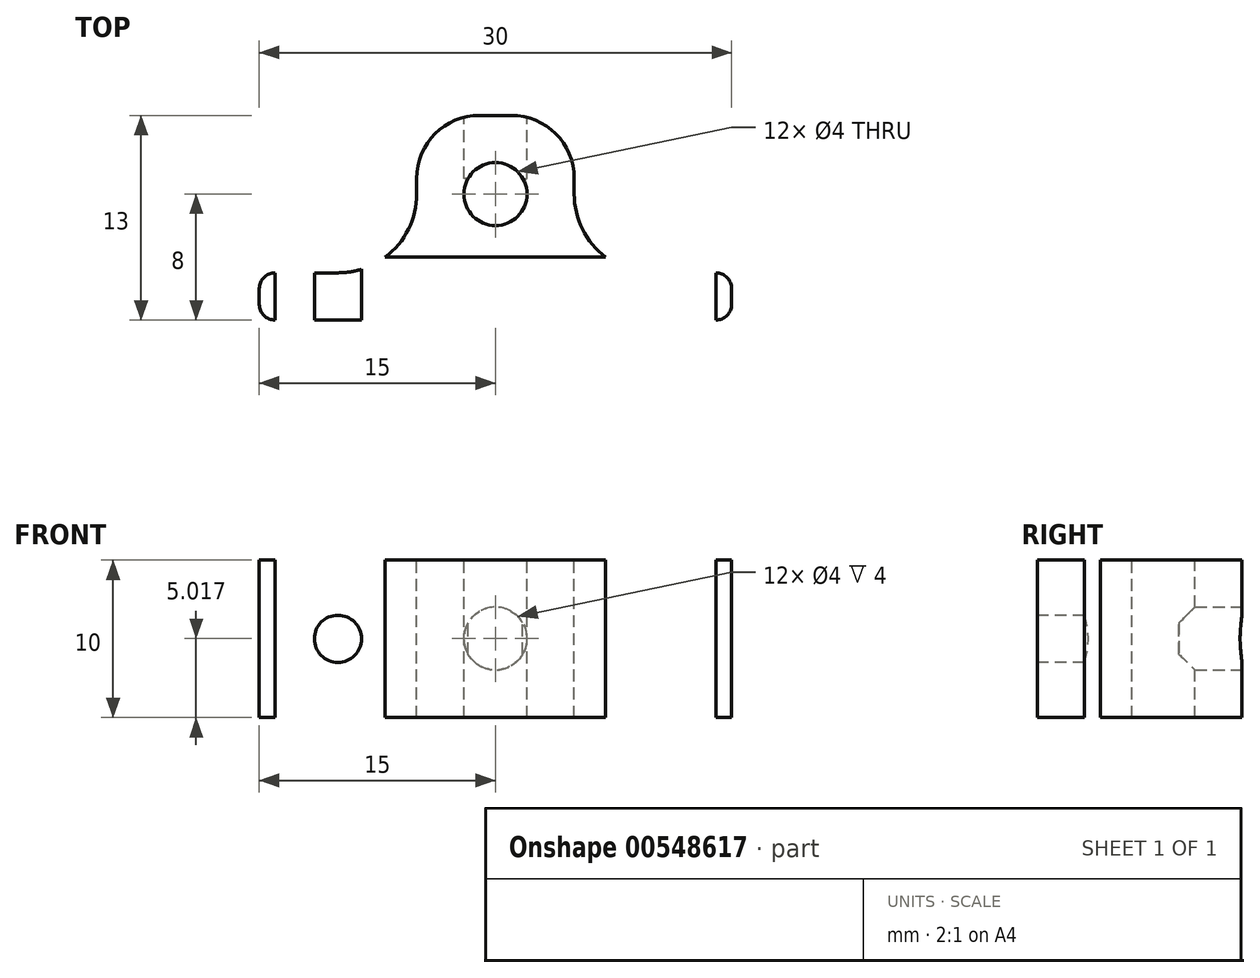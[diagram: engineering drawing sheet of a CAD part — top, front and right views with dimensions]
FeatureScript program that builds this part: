
annotation { "Feature Type Name" : "Feature", "Feature Type Description" : "" }
export const myFeature = defineFeature(function(context is Context, id is Id, definition is map)
    precondition{}
    {
        {
            var Q0;
            Q0=qCreatedBy(makeId("Top.planeOp"),FACE);
            var sketch = newSketch(context, id + "F0", { "sketchPlane" : qUnion([Q0])});
            skLineSegment(sketch, "E0.bottom", {"start": v(14, -1.5) * mm, "end": v(-14, -1.5) * mm});
            skLineSegment(sketch, "E0.top", {"start": v(14, 1.5) * mm, "end": v(10, 1.5) * mm});
            skLineSegment(sketch, "E0.left", {"start": v(15, -0.5) * mm, "end": v(15, 0.5) * mm});
            skLineSegment(sketch, "E0.right", {"start": v(-15, -0.5) * mm, "end": v(-15, 0.5) * mm});
            skPoint(sketch, "E0.middle", {"position": v(0, 0) * mm});
            skPoint(sketch, "E1.visualSharp", {"position": v(-15, 1.5) * mm});
            skArc(sketch, "E1.filletArc", {"start": v(-14, 1.5) * mm, "mid": v(-14.7, 1.2) * mm, "end": v(-15, 0.5) * mm});
            skPoint(sketch, "E2.visualSharp", {"position": v(-15, -1.5) * mm});
            skArc(sketch, "E2.filletArc", {"start": v(-15, -0.5) * mm, "mid": v(-14.7, -1.2) * mm, "end": v(-14, -1.5) * mm});
            skPoint(sketch, "E3.visualSharp", {"position": v(15, -1.5) * mm});
            skArc(sketch, "E3.filletArc", {"start": v(14, -1.5) * mm, "mid": v(14.7, -1.2) * mm, "end": v(15, -0.5) * mm});
            skPoint(sketch, "E4.visualSharp", {"position": v(15, 1.5) * mm});
            skArc(sketch, "E4.filletArc", {"start": v(15, 0.5) * mm, "mid": v(14.7, 1.2) * mm, "end": v(14, 1.5) * mm});
            skLineSegment(sketch, "E5.top", {"start": v(1, 11.5) * mm, "end": v(-1, 11.5) * mm});
            skLineSegment(sketch, "E5.left", {"start": v(5, 6.5) * mm, "end": v(5, 7.5) * mm});
            skLineSegment(sketch, "E5.right", {"start": v(-5, 6.5) * mm, "end": v(-5, 7.5) * mm});
            skPoint(sketch, "E5.middle", {"position": v(0, 6.5) * mm});
            skLineSegment(sketch, "E6.trimOffspring", {"start": v(-10, 1.5) * mm, "end": v(-14, 1.5) * mm});
            skPoint(sketch, "E7.visualSharp", {"position": v(-5, 1.5) * mm});
            skArc(sketch, "E7.filletArc", {"start": v(-10, 1.5) * mm, "mid": v(-6.46, 2.96) * mm, "end": v(-5, 6.5) * mm});
            skPoint(sketch, "E8.visualSharp", {"position": v(5, 1.5) * mm});
            skArc(sketch, "E8.filletArc", {"start": v(5, 6.5) * mm, "mid": v(6.46, 2.96) * mm, "end": v(10, 1.5) * mm});
            skPoint(sketch, "E9.visualSharp", {"position": v(-5, 11.5) * mm});
            skArc(sketch, "E9.filletArc", {"start": v(-1, 11.5) * mm, "mid": v(-3.83, 10.33) * mm, "end": v(-5, 7.5) * mm});
            skPoint(sketch, "E10.visualSharp", {"position": v(5, 11.5) * mm});
            skArc(sketch, "E10.filletArc", {"start": v(5, 7.5) * mm, "mid": v(3.83, 10.33) * mm, "end": v(1, 11.5) * mm});
            skCircle(sketch, "E11", {"center": v(0, 6.5) * mm, "radius": 2 * mm});
            skSolve(sketch);
        }
        {
            var Q0;
            Q0=makeQuery(id+"F0.imprint","IMPRINT",FACE,{"disambiguationData":[TD([[makeQuery(id+"F0.imprint","IMPRINT",EDGE,{"derivedFrom":sQuery(id+"F0.wireOp",EDGE,"E0.bottom")}),-1.0]])]});
            extrude(context, id + "F1", {"entities" : qUnion([Q0]), "oppositeDirection" : true, "depth" : 10 * mm, "offsetDistance" : 25 * mm});
        }
        {
            var Q0;
            Q0=makeQuery(id+"F1.opExtrude","SWEPT_FACE",FACE,{"disambiguationData":[OSD([sQuery(id+"F0.wireOp",EDGE,"E5.top")])]});
            var sketch = newSketch(context, id + "F2", { "sketchPlane" : qUnion([Q0])});
            skCircle(sketch, "E12", {"center": v(0, -4.98) * mm, "radius": 2 * mm});
            skPoint(sketch, "E12.centerSnap0", {"position": v(0, -10) * mm});
            skSolve(sketch);
        }
        {
            var Q0;
            Q0 = qSketchRegion(id + "F2", true);
            extrude(context, id + "F3", {"entities" : qUnion([Q0]), "operationType" : NewBodyOperationType.REMOVE, "oppositeDirection" : true, "depth" : 4 * mm, "offsetDistance" : 25 * mm});
        }
        {
            var Q0;
            Q0=makeQuery(id+"F1.opExtrude","SWEPT_FACE",FACE,{"disambiguationData":[OSD([sQuery(id+"F0.wireOp",EDGE,"E0.bottom")])]});
            var sketch = newSketch(context, id + "F4", { "sketchPlane" : qUnion([Q0])});
            skCircle(sketch, "E13", {"center": v(10, -5) * mm, "radius": 1.5 * mm});
            skLineSegment(sketch, "E14", {"start": v(10, -10) * mm, "end": v(10, 0) * mm, "construction": true});
            skCircle(sketch, "E15.MirrorC", {"center": v(-10, -5) * mm, "radius": 1.5 * mm});
            skSolve(sketch);
        }
        {
            var Q0;
            Q0=makeQuery(id+"F4.imprint","IMPRINT",FACE,{"disambiguationData":[TD([[makeQuery(id+"F4.imprint","IMPRINT",EDGE,{"derivedFrom":sQuery(id+"F4.wireOp",EDGE,"E13")}),1.0]])]});
            var Q1;
            Q1=makeQuery(id+"F4.imprint","IMPRINT",FACE,{"disambiguationData":[TD([[makeQuery(id+"F4.imprint","IMPRINT",EDGE,{"derivedFrom":sQuery(id+"F4.wireOp",EDGE,"E15.MirrorC")}),-1.0]])]});
            var Q2;
            Q2=sQuery(id+"F4.wireOp",EDGE,"E13");
            var Q3;
            Q3=sQuery(id+"F4.wireOp",EDGE,"E15.MirrorC");
            extrude(context, id + "F5", {"entities" : qUnion([Q0, Q1]), "operationType" : NewBodyOperationType.REMOVE, "surfaceEntities" : qUnion([Q2, Q3]), "oppositeDirection" : true, "depth" : 4 * mm, "offsetDistance" : 25 * mm});
        }
    });
